# Revit family: Rohrschelle Titan HD, 1 Zoll, Gummi
name_source: partatom
category: HLS-Bauteile
revit_build: Autodesk Revit 2017 (Build: 20190507_1515(x64)
units: mm (PartAtom-declared; Revit-internal decimal feet)

## family parameters
Arbeitsebenenbasiert = Ja
Beim Laden mit Abzugskörper schneiden = Nein
Bemaßung runder Anschluss = Durchmesser verwenden
Gemeinsam genutzt = Ja
Immer vertikal = Nein
Raumberechnungspunkt = Nein
Teiletyp = Normal

## types (30) — shared parameters
A = 31 mm  [stored 0.101706 ft]
Anschluss = 1''
Anschlußhöhe = 31 mm
Bauart = zweiteilig
Baustoffklasse = B2
Brandschutz = RAL GZ 656
DF1 = 29 mm  [stored 0.0951444 ft]
DS = 6 mm  [stored 0.019685 ft]
DVS = 13 mm
Dämmstärke = 6 mm  [stored 0.019685 ft]
Fabrikat = MEFA
Farbe Schalldämmeinlage = schwarz
Firma = MEFA Befestigungs- und Montagesysteme GmbH
HGA = 20 mm  [stored 0.0656168 ft]
Kurztext1 = Rohrschelle Titan HD 50x5,0
MB = 50 mm  [stored 0.164042 ft]
MD = 5 mm  [stored 0.0164042 ft]
Material = Stahl
Material Schalldämmeinlage = TPE
Materialmaße = 50x5,0 mm
Materialname = S235
Mengeneinheit = St
Oberflaeche = galvanisch verzinkt
Schalldämmeinlage = Gummi
Verschluss = Schraubverschluss
Verschluss-Schraube = M12
Vorgabe-Ansicht = 1219 mm
max. Temperaturbeständigkeit = 100 °C
max. zul. Last horizontal = 0.00 kN
max. zul. Last vertikal = 0.00 kN
vpe = 1 St
zero-valued in all types: Nennweite DN Rohr, Stärke Material, max. Rohraußendurchmesser, min. Rohraußendurchmesser

## per-type parameters (varying)
| type | Achsabstand | Artikelnummer | B | Breite | D | D0 | DF2 | EAN | Gewicht | Gewicht pro Bauteil | H | Höhe | Kurztext2 | R | RM | Rohraußendurchmesser | Rohraußendurchmesser Zoll | S | max. Höhe | max. zul. Last |
| Titan HD, 1", Ø 64, Gummi | 125 mm | 0074507 | 154 mm | 154 mm | 64 mm  [stored 0.209974 ft] | 76 mm  [stored 0.249344 ft] | 19 mm  [stored 0.062336 ft] | 4250928404343 | 0.98 kg | 0.98 kg | 106 mm | 106 mm | 64 mm 1'' TPE | 38 mm  [stored 0.124672 ft] | 43 mm | 64 mm  [stored 0.209974 ft] | Zoll | 125 mm | 106 mm | 3.20 kN |
| Titan HD, 1", Ø 76, Gummi | 137 mm | 0074511 | 166 mm | 166 mm | 76 mm  [stored 0.249344 ft] | 88 mm  [stored 0.288714 ft] | 19 mm  [stored 0.062336 ft] | 4250928404367 | 1.07 kg | 1.07 kg | 118 mm | 118 mm | 76 mm 1'' TPE | 44 mm  [stored 0.144357 ft] | 49 mm | 76 mm  [stored 0.249344 ft] | 2 1/2 Zoll | 137 mm | 118 mm | 3.20 kN |
| Titan HD, 1", Ø 89, Gummi | 150 mm | 0074513 | 179 mm | 179 mm | 89 mm  [stored 0.291995 ft] | 101 mm | 19 mm  [stored 0.062336 ft] | 4250928404381 | 1.17 kg | 1.17 kg | 131 mm | 131 mm | 89 mm 1'' TPE | 51 mm | 56 mm | 89 mm  [stored 0.291995 ft] | 3 Zoll | 150 mm | 131 mm | 3.20 kN |
| Titan HD, 1", Ø108, Gummi | 170 mm | 0074519 | 199 mm | 199 mm | 108 mm | 120 mm | 20 mm  [stored 0.0656168 ft] | 4250928404398 | 1.31 kg | 1.31 kg | 150 mm | 150 mm | 108 mm 1'' TPE | 60 mm  [stored 0.19685 ft] | 65 mm | 108 mm | Zoll | 170 mm | 150 mm | 3.20 kN |
| Titan HD, 1", Ø110, Gummi | 172 mm | 0074535 | 201 mm | 201 mm | 110 mm | 122 mm | 20 mm  [stored 0.0656168 ft] | 4250928404435 | 1.32 kg | 1.32 kg | 152 mm | 152 mm | 110 mm 1'' TPE | 61 mm  [stored 0.200131 ft] | 66 mm | 110 mm | Zoll | 172 mm | 152 mm | 3.20 kN |
| Titan HD, 1", Ø133, Gummi | 195 mm | 0074608 | 224 mm | 224 mm | 133 mm | 145 mm | 20 mm  [stored 0.0656168 ft] | 4250928404497 | 1.50 kg | 1.50 kg | 175 mm | 175 mm | 133 mm 1'' TPE | 73 mm | 78 mm | 133 mm | Zoll | 195 mm | 175 mm | 3.20 kN |
| Titan HD, 1", Ø135, Gummi | 197 mm | 0074616 | 226 mm | 226 mm | 135 mm | 147 mm | 20 mm  [stored 0.0656168 ft] | 4250928404510 | 1.51 kg | 1.51 kg | 177 mm | 177 mm | 135 mm 1'' TPE | 74 mm | 79 mm | 135 mm | Zoll | 197 mm | 177 mm | 3.20 kN |
| Titan HD, 1", Ø140, Gummi | 202 mm | 0074624 | 231 mm | 231 mm | 140 mm | 152 mm | 20 mm  [stored 0.0656168 ft] | 4250928404527 | 1.55 kg | 1.55 kg | 182 mm | 182 mm | 140 mm 1'' TPE | 76 mm  [stored 0.249344 ft] | 81 mm  [stored 0.265748 ft] | 140 mm | 5 Zoll | 202 mm | 182 mm | 3.20 kN |
| Titan HD, 1", Ø160, Gummi | 222 mm | 0074683 | 251 mm | 251 mm | 160 mm | 172 mm | 20 mm  [stored 0.0656168 ft] | 4250928404558 | 1.70 kg | 1.70 kg | 202 mm | 202 mm | 160 mm 1'' TPE | 86 mm  [stored 0.282152 ft] | 91 mm  [stored 0.298556 ft] | 160 mm | Zoll | 222 mm | 202 mm | 3.20 kN |
| Titan HD, 1", Ø165, Gummi | 227 mm | 0074691 | 256 mm | 256 mm | 165 mm | 177 mm | 20 mm  [stored 0.0656168 ft] | 4250928404589 | 1.74 kg | 1.74 kg | 207 mm | 207 mm | 165 mm 1'' TPE | 89 mm  [stored 0.291995 ft] | 94 mm | 165 mm | 6 Zoll | 227 mm | 207 mm | 3.20 kN |
| Titan HD, 1", Ø168, Gummi | 230 mm | 0074713 | 259 mm | 259 mm | 168 mm | 180 mm | 20 mm  [stored 0.0656168 ft] | 4250928404596 | 1.76 kg | 1.76 kg | 210 mm | 210 mm | 168 mm 1'' TPE | 90 mm | 95 mm | 168 mm | Zoll | 230 mm | 210 mm | 3.20 kN |
| Titan HD, 1", Ø194, Gummi | 257 mm | 0074772 | 286 mm | 286 mm | 194 mm | 206 mm | 20 mm  [stored 0.0656168 ft] | 4250928404633 | 1.95 kg | 1.95 kg | 236 mm | 236 mm | 194 mm 1'' TPE | 103 mm | 108 mm | 194 mm | Zoll | 257 mm | 236 mm | 11.50 kN |
| Titan HD, 1", Ø200, Gummi | 263 mm | 0074780 | 292 mm | 292 mm | 200 mm | 212 mm | 20 mm  [stored 0.0656168 ft] | 4250928404657 | 2.00 kg | 2.00 kg | 242 mm | 242 mm | 200 mm 1'' TPE | 106 mm | 111 mm | 200 mm | Zoll | 263 mm | 242 mm | 11.50 kN |
| Titan HD, 1", Ø210, Gummi | 273 mm | 0074802 | 302 mm | 302 mm | 210 mm | 222 mm | 20 mm  [stored 0.0656168 ft] | 4250928404671 | 2.07 kg | 2.07 kg | 252 mm | 252 mm | 210 mm 1'' TPE | 111 mm | 116 mm | 210 mm | Zoll | 273 mm | 252 mm | 11.50 kN |
| Titan HD, 1", Ø219, Gummi | 282 mm | 0074829 | 311 mm | 311 mm | 219 mm | 231 mm | 20 mm  [stored 0.0656168 ft] | 4250928404695 | 2.14 kg | 2.14 kg | 261 mm | 261 mm | 219 mm 1'' TPE | 116 mm | 121 mm | 219 mm | 8 Zoll | 282 mm | 261 mm | 11.50 kN |
| Titan HD, 1", Ø267, Gummi | 330 mm | 0074896 | 359 mm | 359 mm | 267 mm | 279 mm | 20 mm  [stored 0.0656168 ft] | 4250928404732 | 2.50 kg | 2.50 kg | 309 mm | 309 mm | 267 mm 1'' TPE | 140 mm | 145 mm | 267 mm | Zoll | 330 mm | 309 mm | 11.50 kN |
| Titan HD, 1", Ø273, Gummi | 336 mm | 0074918 | 365 mm | 365 mm | 273 mm | 285 mm | 20 mm  [stored 0.0656168 ft] | 4250928404756 | 2.55 kg | 2.55 kg | 315 mm | 315 mm | 273 mm 1'' TPE | 143 mm | 148 mm | 273 mm | 10 Zoll | 336 mm | 315 mm | 11.50 kN |
| Titan HD, 1", Ø324, Gummi | 387 mm | 0074942 | 416 mm | 416 mm | 324 mm | 336 mm | 20 mm  [stored 0.0656168 ft] | 4250928404794 | 2.93 kg | 2.93 kg | 366 mm | 366 mm | 324 mm 1'' TPE | 168 mm | 173 mm | 324 mm | 12 Zoll | 387 mm | 366 mm | 11.50 kN |
| Titan HD, 1", Ø356, Gummi | 419 mm | 0074969 | 448 mm | 448 mm | 356 mm | 368 mm | 20 mm  [stored 0.0656168 ft] | 4250928404817 | 3.17 kg | 3.17 kg | 398 mm | 398 mm | 356 mm 1'' TPE | 184 mm | 189 mm | 356 mm | Zoll | 419 mm | 398 mm | 11.50 kN |
| Titan HD, 1", Ø368, Gummi | 431 mm | 0074985 | 460 mm | 460 mm | 368 mm | 380 mm | 20 mm  [stored 0.0656168 ft] | 4250928404831 | 3.26 kg | 3.26 kg | 410 mm | 410 mm | 368 mm 1'' TPE | 190 mm | 195 mm | 368 mm | Zoll | 431 mm | 410 mm | 11.50 kN |
| Titan HD, 1", Ø114, Gummi | 176 mm | 0074551 | 205 mm | 205 mm | 114 mm | 126 mm | 20 mm  [stored 0.0656168 ft] | 4250928404442 | 1.35 kg | 1.35 kg | 156 mm | 156 mm | 114 mm 1'' TPE | 63 mm  [stored 0.206693 ft] | 68 mm  [stored 0.223097 ft] | 114 mm | 4 Zoll | 176 mm | 156 mm | 3.20 kN |
| Titan HD, 1", Ø125, Gummi | 187 mm | 0074586 | 216 mm | 216 mm | 125 mm | 137 mm | 20 mm  [stored 0.0656168 ft] | 4250928404459 | 1.44 kg | 1.44 kg | 167 mm | 167 mm | 125 mm 1'' TPE | 69 mm | 74 mm | 125 mm | Zoll | 187 mm | 167 mm | 3.20 kN |
| Titan HD, 1", Ø127, Gummi | 189 mm | 0074594 | 218 mm | 218 mm | 127 mm | 139 mm | 20 mm  [stored 0.0656168 ft] | 4250928404473 | 1.45 kg | 1.45 kg | 169 mm | 169 mm | 127 mm 1'' TPE | 70 mm | 75 mm | 127 mm | Zoll | 189 mm | 169 mm | 3.20 kN |
| Titan HD, 1", Ø152, Gummi | 214 mm | 0074640 | 243 mm | 243 mm | 152 mm | 164 mm | 20 mm  [stored 0.0656168 ft] | 4250928404534 | 1.64 kg | 1.64 kg | 194 mm | 194 mm | 152 mm 1'' TPE | 82 mm  [stored 0.269029 ft] | 87 mm  [stored 0.285433 ft] | 152 mm | Zoll | 214 mm | 194 mm | 3.20 kN |
| Titan HD, 1", Ø177, Gummi | 239 mm | 0074748 | 268 mm | 268 mm | 177 mm | 189 mm | 20 mm  [stored 0.0656168 ft] | 4250928404602 | 1.83 kg | 1.83 kg | 219 mm | 219 mm | 177 mm 1'' TPE | 95 mm | 100 mm | 177 mm | Zoll | 239 mm | 219 mm | 11.50 kN |
| Titan HD, 1", Ø180, Gummi | 242 mm | 0074756 | 271 mm | 271 mm | 180 mm | 192 mm | 20 mm  [stored 0.0656168 ft] | 4250928404619 | 1.85 kg | 1.85 kg | 222 mm | 222 mm | 180 mm 1'' TPE | 96 mm | 101 mm | 180 mm | Zoll | 242 mm | 222 mm | 11.50 kN |
| Titan HD, 1", Ø225, Gummi | 288 mm | 0074845 | 317 mm | 317 mm | 225 mm | 237 mm | 20 mm  [stored 0.0656168 ft] | 4250928404701 | 2.19 kg | 2.19 kg | 267 mm | 267 mm | 225 mm 1'' TPE | 119 mm | 124 mm | 225 mm | Zoll | 288 mm | 267 mm | 11.50 kN |
| Titan HD, 1", Ø245, Gummi | 308 mm | 0074861 | 337 mm | 337 mm | 245 mm | 257 mm | 20 mm  [stored 0.0656168 ft] | 4250928404718 | 2.34 kg | 2.34 kg | 287 mm | 287 mm | 245 mm 1'' TPE | 129 mm | 134 mm | 245 mm | Zoll | 308 mm | 287 mm | 11.50 kN |
| Titan HD, 1", Ø280, Gummi | 343 mm | 0074926 | 372 mm | 372 mm | 280 mm | 292 mm | 20 mm  [stored 0.0656168 ft] | 4250928404763 | 2.60 kg | 2.60 kg | 322 mm | 322 mm | 280 mm 1'' TPE | 146 mm | 151 mm | 280 mm | Zoll | 343 mm | 322 mm | 11.50 kN |
| Titan HD, 1", Ø298, Gummi | 361 mm | 0074934 | 390 mm | 390 mm | 298 mm | 310 mm | 20 mm  [stored 0.0656168 ft] | 4250928404770 | 2.73 kg | 2.73 kg | 340 mm | 340 mm | 298 mm 1'' TPE | 155 mm | 160 mm | 298 mm | Zoll | 361 mm | 340 mm | 11.50 kN |

note: [stored X ft] marks values corroborated as IEEE doubles in the binary element streams (Revit-internal decimal feet)

## geometry (parser evidence)
native form markers: Sweep x6
no freeform markers — native parametric forms only
